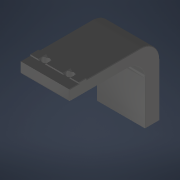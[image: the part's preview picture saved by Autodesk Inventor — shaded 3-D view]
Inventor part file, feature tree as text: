
AUTODESK INVENTOR PART (.ipt)
format: ipt  version: 2022.1 (Build 261234000, 234)  size: 290,816 bytes
history: native  units: mm
features: direct_edit x2, delete_face x2, move_body x2, chamfer x1, hole x1, sketch x1, other x1
ambient origin geometry x8: Origin, YZ Plane, XZ Plane, XY Plane, X Axis, Y Axis, Z Axis, Center Point
bodies: Volumenkörper1 (feature_tree)
feature tree (10):
  direct_edit  "Direktbearbeitung1"
  delete_face  "Fläche löschen1"
  chamfer  "Fase1"  Distance=3.0mm
  hole  "Bohrung1"  [1 undecoded]
  delete_face  "Fläche löschen2"
  direct_edit  "Direktbearbeitung2"
  sketch  "Skizze1"  dims[d3=0.8mm d4=2.0mm d5=45.0deg d6=8.6mm d7=6.0mm d8=4.0mm d9=2.0mm d10=90.0deg d11=3.0mm d12=0.0mm d13=0.0mm d14=0.0mm d15=6.0mm]
  other  "Dock Fixed Mount"
  move_body  "Verschieben1"
  move_body  "Verschieben2"
note: 1 required parameter value undecoded (feature->parameter linkage not recoverable at this tier; creation-order binding heuristic only, values carry confidence <= 0.55)
